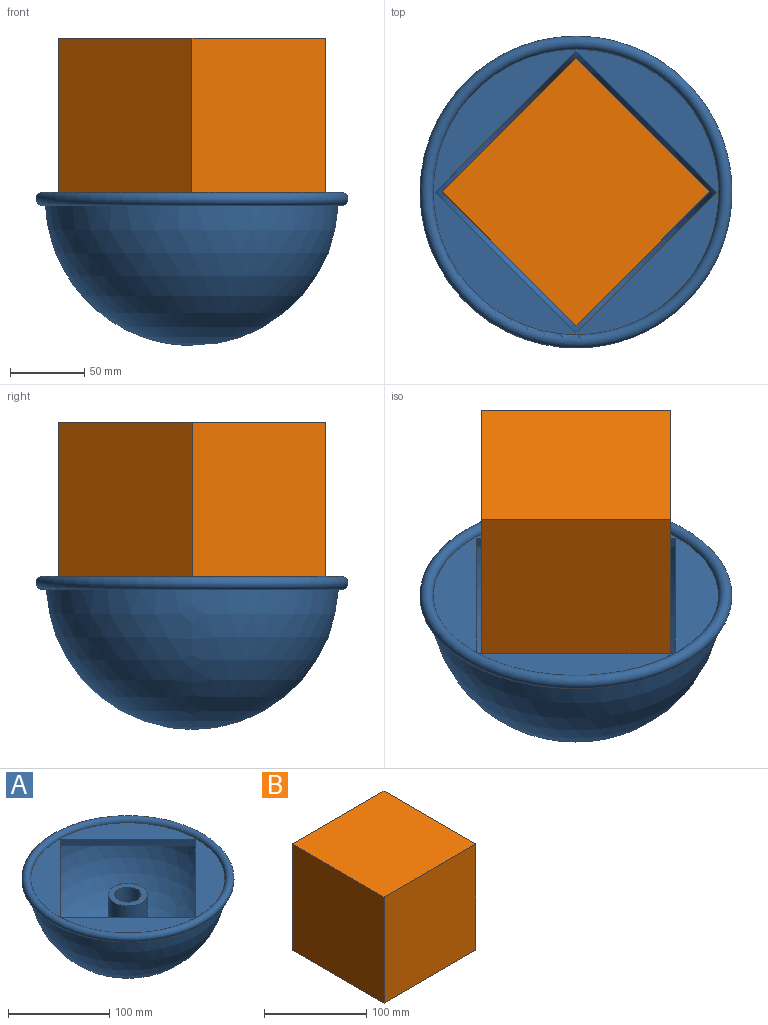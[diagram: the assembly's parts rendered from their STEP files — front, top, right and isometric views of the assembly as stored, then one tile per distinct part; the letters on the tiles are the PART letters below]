
ASSEMBLY  parts=2 mates=1
PART A: 13 faces, bbox 226.9x226.9x102.9 mm
  f0: plane 191.81x191.81mm, normal (0,0,1), area 11112.8mm2, adj f5,f6,f7,f8,f11
  f1: sphere r=95.27mm, area 52043.4mm2, adj f3,f4
  f2: plane 38.61x38.61mm, normal (0,0,1), area 643.5mm2, adj f3,f9
  f3: cylinder r=19.3mm len=74.24mm, axis (0,0,-1), area 9005mm2, adj f1,f2
  f4: plane 190.11x190.11mm, normal (0,0,-1), area 10604.8mm2, adj f1,f5,f6,f7,f8
  f5: plane 94.29x94.29mm, normal (-0.71,0.71,0), area 846.8mm2, adj f0,f4,f6,f8
  f6: plane 94.29x94.29mm, normal (0.71,0.71,0), area 846.8mm2, adj f0,f4,f5,f7
  f7: plane 94.29x94.29mm, normal (0.71,-0.71,0), area 846.8mm2, adj f0,f4,f6,f8
  f8: plane 94.29x94.29mm, normal (-0.71,-0.71,0), area 846.8mm2, adj f0,f4,f5,f7
  f9: cylinder r=12.95mm len=50.8mm, axis (0,0,1), area 4134.7mm2, adj f2,f10
  f10: plane 25.91x25.91mm, normal (0,0,1), area 527.2mm2, adj f9
  f11: torus R=100.35mm, axis (0,0,-1), area 14615.8mm2, adj f0,f12
  f12: sphere r=98.44mm, area 58431.9mm2, adj f11
PART B: 6 faces, bbox 127x127x127 mm
  f0: plane 127x127mm, normal (-1,0,0), area 16129mm2, adj f1,f3,f4,f5
  f1: plane 127x127mm, normal (0,-1,0), area 16129mm2, adj f0,f2,f4,f5
  f2: plane 127x127mm, normal (1,0,0), area 16129mm2, adj f1,f3,f4,f5
  f3: plane 127x127mm, normal (0,1,0), area 16129mm2, adj f0,f2,f4,f5
  f4: plane 127x127mm, normal (0,0,1), area 16129mm2, adj f0,f1,f2,f3
  f5: plane 127x127mm, normal (0,0,-1), area 16129mm2, adj f0,f1,f2,f3
PLACE A t=(129.17,-3.09,-63.23)mm
PLACE B rot(axis=(0,0,-1),45deg) t=(39.37,-3.09,-82.28)mm fixed
MATE revolute A.f3 <-> B.f5  axis (0,0,1) through (129.17,-3.09,-82.28)mm
